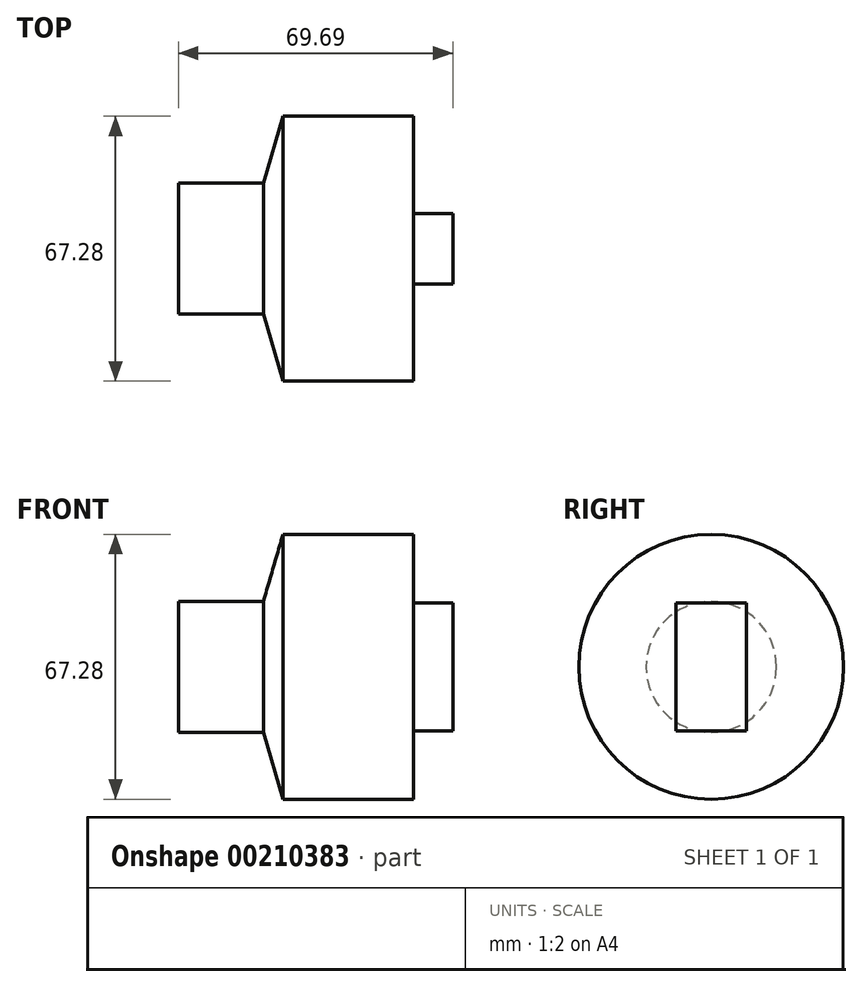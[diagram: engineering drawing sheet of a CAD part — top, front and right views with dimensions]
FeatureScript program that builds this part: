
annotation { "Feature Type Name" : "Feature", "Feature Type Description" : "" }
export const myFeature = defineFeature(function(context is Context, id is Id, definition is map)
    precondition{}
    {
        {
            var Q0;
            Q0=qCreatedBy(makeId("Front.planeOp"),FACE);
            var sketch = newSketch(context, id + "F0", { "sketchPlane" : qUnion([Q0])});
            skLineSegment(sketch, "E0", {"start": v(0, 0) * mm, "end": v(59.69, 0) * mm});
            skLineSegment(sketch, "E1", {"start": v(59.69, 0) * mm, "end": v(59.69, 33.64) * mm});
            skLineSegment(sketch, "E2", {"start": v(59.69, 33.64) * mm, "end": v(26.51, 33.64) * mm});
            skLineSegment(sketch, "E3", {"start": v(26.51, 33.64) * mm, "end": v(21.55, 16.59) * mm});
            skLineSegment(sketch, "E4", {"start": v(21.55, 16.59) * mm, "end": v(0, 16.59) * mm});
            skLineSegment(sketch, "E5", {"start": v(0, 16.59) * mm, "end": v(0, 0) * mm});
            skSolve(sketch);
        }
        {
            var Q0;
            Q0 = qSketchRegion(id + "F0", true);
            var Q1;
            Q1=sQuery(id+"F0.wireOp",EDGE,"E0");
            revolve(context, id + "F1", {"entities" : qUnion([Q0]), "axis" : qUnion([Q1]), "revolveType" : RevolveType.FULL});
        }
        {
            var Q0;
            Q0=makeQuery(id+"F1.opRevolve","SWEPT_FACE",FACE,{"disambiguationData":[OSD([sQuery(id+"F0.wireOp",EDGE,"E1")])]});
            var sketch = newSketch(context, id + "F2", { "sketchPlane" : qUnion([Q0])});
            skLineSegment(sketch, "E6.bottom", {"start": v(8.95, 16.3) * mm, "end": v(-8.95, 16.3) * mm});
            skLineSegment(sketch, "E6.top", {"start": v(8.95, -16.3) * mm, "end": v(-8.95, -16.3) * mm});
            skLineSegment(sketch, "E6.left", {"start": v(8.95, 16.3) * mm, "end": v(8.95, -16.3) * mm});
            skLineSegment(sketch, "E6.right", {"start": v(-8.95, 16.3) * mm, "end": v(-8.95, -16.3) * mm});
            skPoint(sketch, "E6.middle", {"position": v(0, 0) * mm});
            skSolve(sketch);
        }
        {
            var Q0;
            Q0 = qSketchRegion(id + "F2", true);
            extrude(context, id + "F3", {"entities" : qUnion([Q0]), "operationType" : NewBodyOperationType.ADD, "depth" : 10 * mm, "offsetDistance" : 25.4 * mm});
        }
    });
